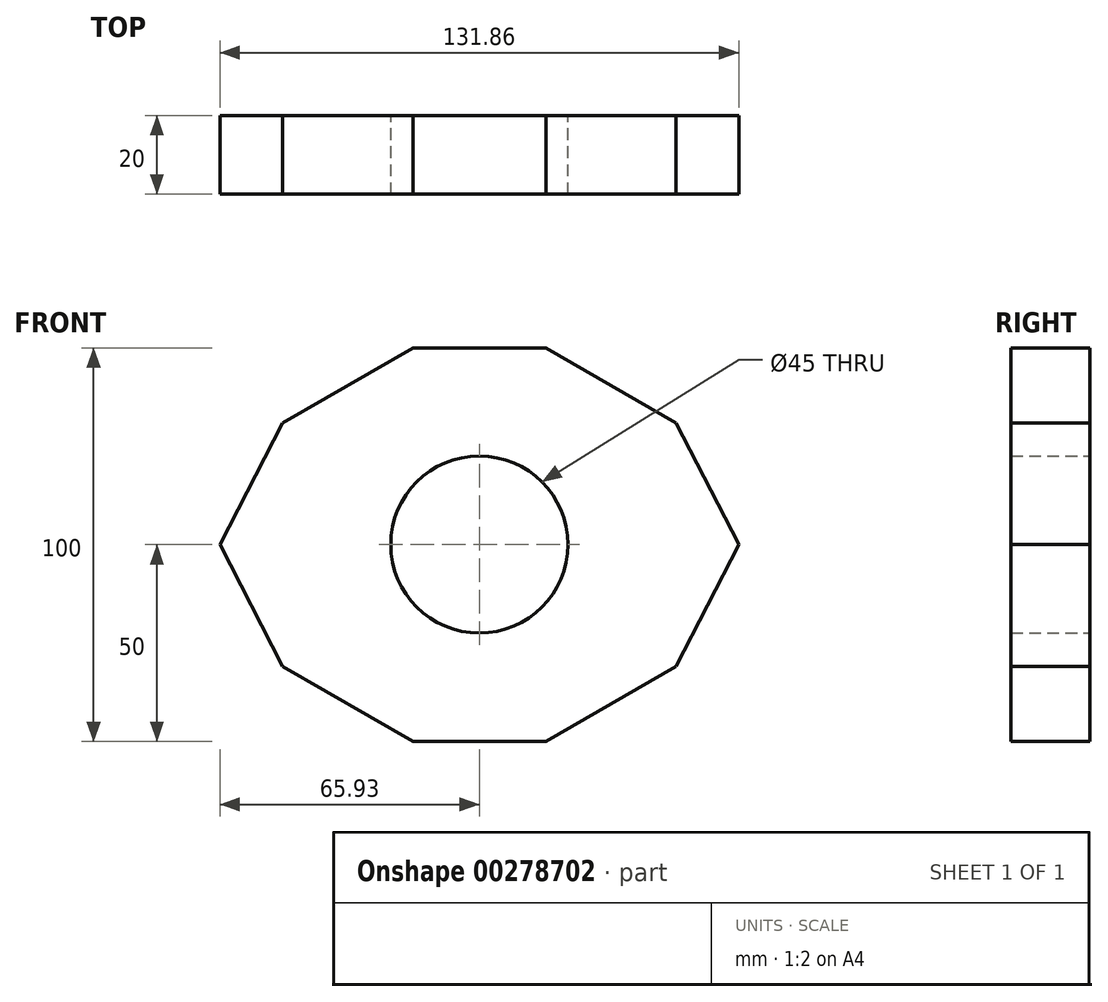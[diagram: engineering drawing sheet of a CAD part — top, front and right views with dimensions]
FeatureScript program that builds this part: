
annotation { "Feature Type Name" : "Feature", "Feature Type Description" : "" }
export const myFeature = defineFeature(function(context is Context, id is Id, definition is map)
    precondition{}
    {
        {
            var Q0;
            Q0=qCreatedBy(makeId("Front.planeOp"),FACE);
            var sketch = newSketch(context, id + "F0", { "sketchPlane" : qUnion([Q0])});
            skLineSegment(sketch, "E0.bottom", {"start": v(-16.9, 50) * mm, "end": v(16.9, 50) * mm});
            skLineSegment(sketch, "E0.top", {"start": v(-16.9, -50) * mm, "end": v(16.9, -50) * mm});
            skLineSegment(sketch, "E0.left", {"start": v(-50, 30.94) * mm, "end": v(-50, -30.94) * mm});
            skLineSegment(sketch, "E0.right", {"start": v(50, 30.94) * mm, "end": v(50, -30.94) * mm});
            skPoint(sketch, "E1.visualSharp", {"position": v(-50, 50) * mm});
            skLineSegment(sketch, "E1.filletArc", {"start": v(-50, 50) * mm, "end": v(-50, 50) * mm});
            skPoint(sketch, "E2.visualSharp", {"position": v(50, 50) * mm});
            skLineSegment(sketch, "E2.filletArc", {"start": v(50, 50) * mm, "end": v(50, 50) * mm});
            skPoint(sketch, "E3.visualSharp", {"position": v(50, -50) * mm});
            skLineSegment(sketch, "E3.filletArc", {"start": v(50, -50) * mm, "end": v(50, -50) * mm});
            skPoint(sketch, "E4.visualSharp", {"position": v(-50, -50) * mm});
            skLineSegment(sketch, "E4.filletArc", {"start": v(-50, -50) * mm, "end": v(-50, -50) * mm});
            skCircle(sketch, "E5", {"center": v(0, 0) * mm, "radius": 22.5 * mm});
            skLineSegment(sketch, "E6.1", {"start": v(-68.26, -4.53) * mm, "end": v(-50, 30.94) * mm});
            skPoint(sketch, "E6.0.midPoint", {"position": v(-59.13, 22.74) * mm});
            skLineSegment(sketch, "E7", {"start": v(-50, 30.94) * mm, "end": v(-16.9, 50) * mm});
            skLineSegment(sketch, "E8.MirrorCS", {"start": v(50, 30.94) * mm, "end": v(16.9, 50) * mm});
            skLineSegment(sketch, "E9.MirrorCS", {"start": v(68.26, -4.53) * mm, "end": v(50, 30.94) * mm});
            skPoint(sketch, "E10.MirrorP", {"position": v(59.13, 22.74) * mm});
            skLineSegment(sketch, "E11.MirrorCS", {"start": v(-50, -30.94) * mm, "end": v(-50, -40.47) * mm});
            skLineSegment(sketch, "E12.MirrorCS", {"start": v(-68.26, 4.53) * mm, "end": v(-50, -30.94) * mm});
            skPoint(sketch, "E13.MirrorP", {"position": v(-59.13, -22.74) * mm});
            skLineSegment(sketch, "E14.MirrorCS", {"start": v(-50, -30.94) * mm, "end": v(-16.9, -50) * mm});
            skLineSegment(sketch, "E15.MirrorCS", {"start": v(68.26, 4.53) * mm, "end": v(50, -30.94) * mm});
            skPoint(sketch, "E16.MirrorP", {"position": v(59.13, -22.74) * mm});
            skLineSegment(sketch, "E17.MirrorCS", {"start": v(50, -30.94) * mm, "end": v(16.9, -50) * mm});
            skSolve(sketch);
        }
        {
            var Q0;
            Q0=qSketchRegion(id+"F0",true);
            extrude(context, id + "F1", {"entities" : qUnion([Q0]), "depth" : 20 * mm});
        }
    });
